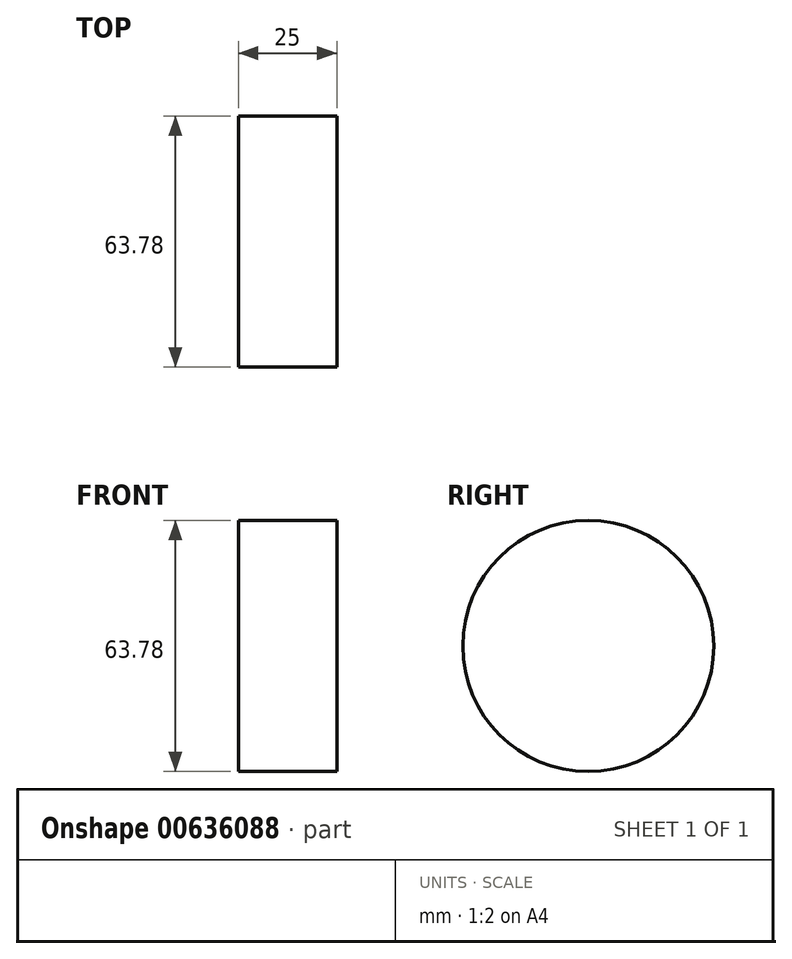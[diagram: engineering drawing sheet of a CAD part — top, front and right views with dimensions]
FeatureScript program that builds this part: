
annotation { "Feature Type Name" : "Feature", "Feature Type Description" : "" }
export const myFeature = defineFeature(function(context is Context, id is Id, definition is map)
    precondition{}
    {
        {
            var Q0;
            Q0=qCreatedBy(makeId("Right.planeOp"),FACE);
            var sketch = newSketch(context, id + "F0", { "sketchPlane" : qUnion([Q0])});
            skCircle(sketch, "E0", {"center": v(0, 0) * mm, "radius": 31.9 * mm});
            skSolve(sketch);
        }
        {
            var Q0;
            Q0 = qSketchRegion(id + "F0", true);
            extrude(context, id + "F1", {"entities" : qUnion([Q0]), "depth" : 25 * mm, "offsetDistance" : 25 * mm});
        }
    });
